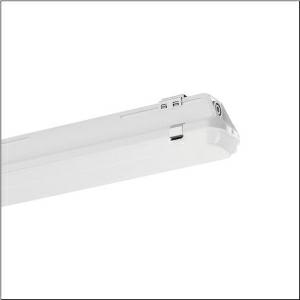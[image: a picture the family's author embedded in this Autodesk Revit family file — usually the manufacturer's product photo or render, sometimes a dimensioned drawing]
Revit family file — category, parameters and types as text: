
# Revit family: monsun_r__11_51fp10fp460l_0793
name_source: partatom
category: Lighting Fixtures
units: mm (PartAtom-declared; Revit-internal decimal feet)

## family parameters
Cut with Voids When Loaded = No
Host = Face
Light Source = No
Part Type = Normal
Room Calculation Point = No
Round Connector Dimension = Use Diameter
Shared = No

## types (1)
- --- (1 x LED, 6050 lm, 31.5 W, 4000K)
    Apparent Load = 32 VA
    CIE Flux Codes = 47 77 93 94 100
    Color Rendering = 80
    Color Temperature = 4000K
    Default Elevation = 1800 mm
    Description = Monsun® 11, damp-proof luminaire, chain hanger, primary optical cover: enclosure, of PMMA, light emission: direct distribution, primary light characteristic: symmetric, installation type: suspended mounting, surface-mounted, horizontal mounting, vertical mounting, LED, rated luminous flux: 6.050lm, luminous efficacy: 192lm/W, light colour: 840, colour temperature: 4000K, control gear: DALI 2, CLO, with terminal, 5-pole, max. 2.5mm², mains connection: 220..240V, AC, 50/60Hz, rated input power: 32W, luminaire housing, of glass-fibre reinforced polyester, uncoated, bright grey, incl. chain hanger, length: 1.590mm, width: 90mm, height: 88mm, clip for enclosure, of stainless steel (V2A), ceiling mounting element, of stainless steel (V2A), chain hanger, of stainless steel (V2A), protection rating (complete): IP66, insulation class (complete): insulation class I (protective earthing), certification: CE, ENEC, VDE, UKCA, protection symbol: D, impact resistance: IK04, permissible operating ambient temperature: -25..+40°C, standard: EN 50419, EN 60598-2-1, corresponds to IFS (International Featured Standards) requirements for safety and quality in the food industry, for indoor or canopied outdoor use, no direct snow, no direct sun, no direct rain, LABS conformity tested according to VDMA 24364:2018-05, contact your sales advisor before using the luminaires in applications with unclear chemical exposure, large temperature fluctuations or condensation-forming humidity, packaging unit: 1 piece
    Height = 89 mm
    Lamp = 1 x LED
    Lamp Light Flux = 6050 lm
    Lamp Power = 31.5 W
    Lamp count = 1
    Length = 1590 mm
    Luminous efficacy = 192 lm/W
    Manufacturer = Siteco
    ModVariant = No
    Model = 51FP10FP460L
    Mounting Place = Ceiling
    Mounting Type = Surface mounted
    Number of Poles = 1
    OnlyDefault = Yes
    Power Factor = 1
    Product Name = Monsun® 11
    Product group = damp-proof luminaire
    ProductGroupID = 300
    Protection Class = Protection class I
    Protection Degree = IP 66
    RLX_Detail_Level = 1
    RLX_Emergency_Light_Flux = 0 lm
    RLX_Emergency_Type = 0
    RLX_Emergency_Type_DB = No
    RlxData = <blob elided: 92617 chars, md5=52d6912c>
    Socket = socket
    Standby Power = 0 W
    System Light Flux = 6050 lm
    System Power = 32 W
    Type Comments = factory setting: luminous flux: 100 % | dim-lin: 254 | 219 mA
    Type Image = l_1349237.jpg
    URL = http://relux.com
    VarID = @adj_013671
    Voltage = 0 V
    Weight = 0.00 kg
    Width = 90 mm

## geometry (parser evidence)
native form markers: Blend x4, Sweep x11
no freeform markers — native parametric forms only
